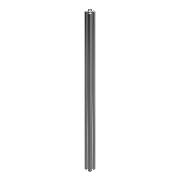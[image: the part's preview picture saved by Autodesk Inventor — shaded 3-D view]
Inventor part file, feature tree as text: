
AUTODESK INVENTOR PART (.ipt)
format: ipt  version: 2018 (Build 220112000, 112)  size: 146,432 bytes
history: native  units: mm
features: extrude x1, sketch x1
ambient origin geometry x8: Origin, YZ Plane, XZ Plane, XY Plane, X Axis, Y Axis, Z Axis, Center Point
bodies: Solid1 (feature_tree)
feature tree (2):
  extrude  "Extrusion1"  [1 undecoded]
  sketch  "Sketch1"  dims[d0=500.0mm d1=0.0mm]
note: 1 required parameter value undecoded (feature->parameter linkage not recoverable at this tier; creation-order binding heuristic only, values carry confidence <= 0.55)
